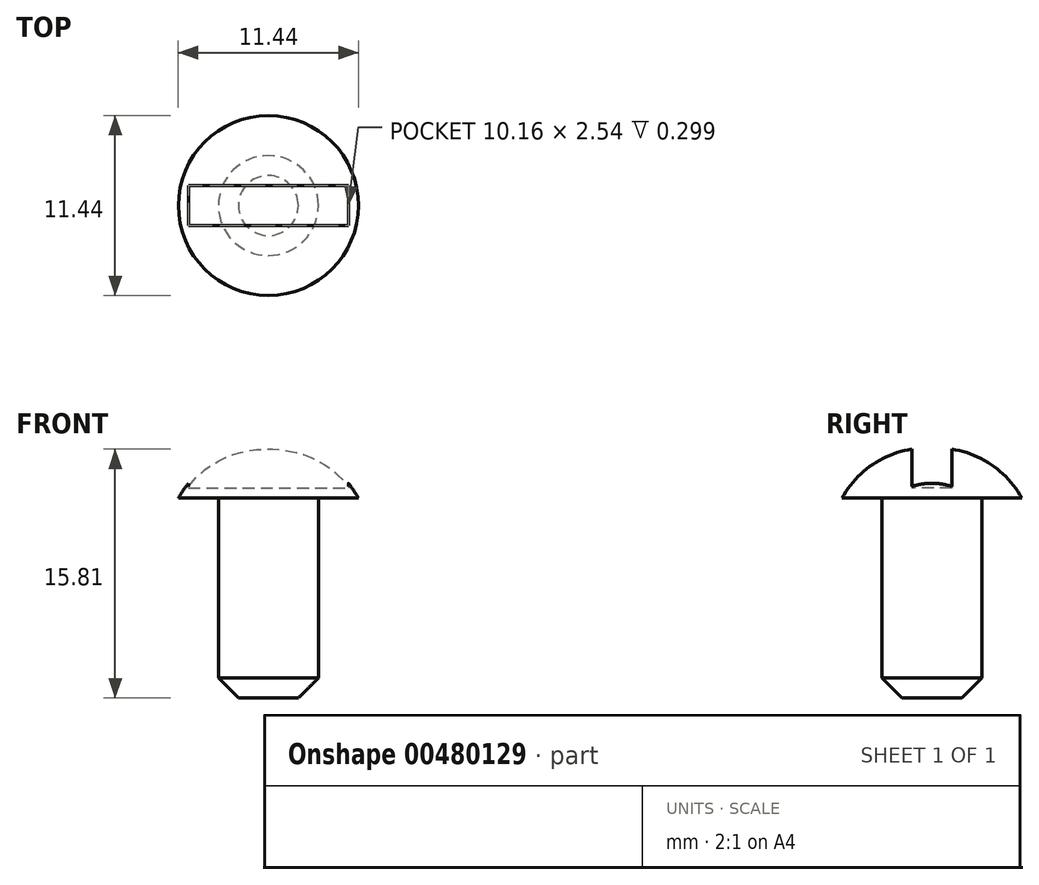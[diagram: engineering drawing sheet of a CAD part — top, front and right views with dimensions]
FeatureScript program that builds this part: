
annotation { "Feature Type Name" : "Feature", "Feature Type Description" : "" }
export const myFeature = defineFeature(function(context is Context, id is Id, definition is map)
    precondition{}
    {
        {
            var Q0;
            Q0=qCreatedBy(makeId("Front.planeOp"),FACE);
            var sketch = newSketch(context, id + "F0", { "sketchPlane" : qUnion([Q0])});
            skLineSegment(sketch, "E0", {"start": v(0, 15.88) * mm, "end": v(0, 0) * mm});
            skLineSegment(sketch, "E1", {"start": v(0, 0) * mm, "end": v(3.17, 0) * mm});
            skLineSegment(sketch, "E2", {"start": v(3.17, 0) * mm, "end": v(3.17, 12.7) * mm});
            skLineSegment(sketch, "E3", {"start": v(3.17, 12.7) * mm, "end": v(5.72, 12.7) * mm});
            skArc(sketch, "E4", {"start": v(5.72, 12.7) * mm, "mid": v(3.31, 15.1) * mm, "end": v(0, 15.88) * mm});
            skSolve(sketch);
        }
        {
            var Q0;
            Q0=makeQuery(id+"F0.imprint","IMPRINT",FACE,{"disambiguationData":[TD([[makeQuery(id+"F0.imprint","IMPRINT",EDGE,{"derivedFrom":sQuery(id+"F0.wireOp",EDGE,"E0")}),1.0]])]});
            var Q1;
            Q1=sQuery(id+"F0.wireOp",EDGE,"E0");
            revolve(context, id + "F1", {"entities" : qUnion([Q0]), "axis" : qUnion([Q1]), "revolveType" : RevolveType.FULL});
        }
        {
            var Q0;
            Q0=makeQuery(id+"F1.opRevolve","SWEPT_EDGE",EDGE,{"disambiguationData":[OSD([sQuery(id+"F0.wireOp",EDGE,"E1"),sQuery(id+"F0.wireOp",EDGE,"E2")])]});
            chamfer(context, id + "F2", {"entities" : qUnion([Q0]), "width" : 1.27 * mm, "tangentPropagation" : true});
        }
        {
            var Q0;
            Q0=makeQuery(id+"F1.opRevolve","SWEPT_FACE",FACE,{"disambiguationData":[OSD([sQuery(id+"F0.wireOp",EDGE,"E3")])]});
            cPlane(context, id + "F3", {"entities" : qUnion([Q0]), "cplaneType" : CPlaneType.OFFSET, "offset" : 0.64 * mm, "oppositeDirection" : true, "width" : 152.4 * mm, "height" : 152.4 * mm});
        }
        {
            var Q0;
            Q0=qCreatedBy(id+"F3.planeOp",FACE);
            var sketch = newSketch(context, id + "F4", { "sketchPlane" : qUnion([Q0])});
            skLineSegment(sketch, "E5.bottom", {"start": v(-5.08, -1.27) * mm, "end": v(5.08, -1.27) * mm});
            skLineSegment(sketch, "E5.top", {"start": v(-5.08, 1.27) * mm, "end": v(5.08, 1.27) * mm});
            skLineSegment(sketch, "E5.left", {"start": v(-5.08, -1.27) * mm, "end": v(-5.08, 1.27) * mm});
            skLineSegment(sketch, "E5.right", {"start": v(5.08, -1.27) * mm, "end": v(5.08, 1.27) * mm});
            skPoint(sketch, "E5.middle", {"position": v(0, 0) * mm});
            skSolve(sketch);
        }
        {
            var Q0;
            Q0 = qSketchRegion(id + "F4", true);
            extrude(context, id + "F5", {"entities" : qUnion([Q0]), "operationType" : NewBodyOperationType.REMOVE, "oppositeDirection" : true, "depth" : 25.4 * mm, "offsetDistance" : 25.4 * mm});
        }
    });
